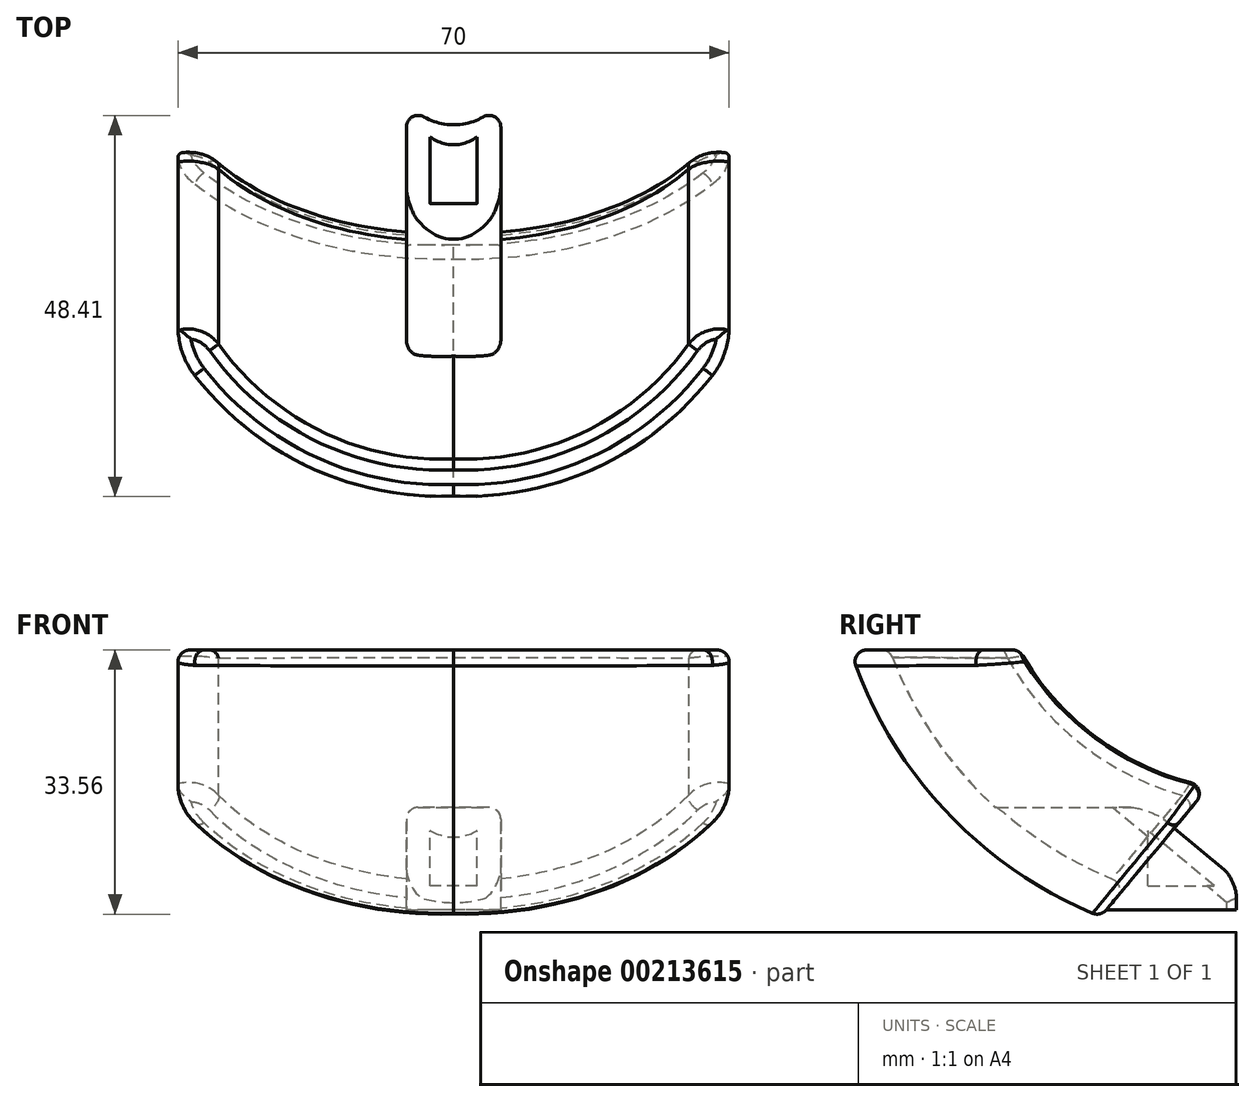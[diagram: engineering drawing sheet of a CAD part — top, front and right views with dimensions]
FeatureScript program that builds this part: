
annotation { "Feature Type Name" : "Feature", "Feature Type Description" : "" }
export const myFeature = defineFeature(function(context is Context, id is Id, definition is map)
    precondition{}
    {
        {
            var Q0;
            Q0=qCreatedBy(makeId("Right.planeOp"),FACE);
            var sketch = newSketch(context, id + "F0", { "sketchPlane" : qUnion([Q0])});
            skLineSegment(sketch, "E0.bottom", {"start": v(0, 0) * mm, "end": v(30, 0) * mm, "construction": true});
            skLineSegment(sketch, "E0.left", {"start": v(0, 0) * mm, "end": v(0, 30) * mm, "construction": true});
            skArc(sketch, "E1", {"start": v(0, 30) * mm, "mid": v(11.66, 11.66) * mm, "end": v(30, 0) * mm});
            skPoint(sketch, "E2", {"position": v(13.08, 10.3) * mm});
            skPoint(sketch, "E3", {"position": v(-15, 30) * mm});
            skPoint(sketch, "E4", {"position": v(3.08, 10.3) * mm});
            skPoint(sketch, "E5", {"position": v(30, 0) * mm});
            skPoint(sketch, "E6", {"position": v(25, 0) * mm});
            skFitSpline(sketch, "E7", {"points": [v(-15, 30) * mm, v(25, 0) * mm, v(100.66, 9.32) * mm], "startDerivative": vector(35.39, -77.1) * mm, "endDerivative": vector(150.07, 40.05) * mm});
            skSolve(sketch);
        }
        {
            var Q0;
            Q0=sQuery(id+"F0.wireOp",VERTEX,"E1.start");
            var Q1;
            Q1=qCreatedBy(makeId("Top.planeOp"),FACE);
            cPlane(context, id + "F1", {"entities" : qUnion([Q0, Q1]), "cplaneType" : CPlaneType.PLANE_POINT, "offset" : 25 * mm, "width" : 150 * mm, "height" : 150 * mm});
        }
        {
            var Q0;
            Q0=qCreatedBy(id+"F1.planeOp",FACE);
            var sketch = newSketch(context, id + "F2", { "sketchPlane" : qUnion([Q0])});
            skArc(sketch, "E8", {"start": v(-35, 24.67) * mm, "mid": v(-21.71, 6.36) * mm, "end": v(0, 0) * mm});
            skArc(sketch, "E9", {"start": v(0, 0) * mm, "mid": v(21.71, 6.36) * mm, "end": v(35, 24.67) * mm});
            skLineSegment(sketch, "E10", {"start": v(-35, 24.67) * mm, "end": v(-35, 16.25) * mm});
            skArc(sketch, "E11.0", {"start": v(0, -5) * mm, "mid": v(18.2, -1.4) * mm, "end": v(32.82, 10.02) * mm});
            skArc(sketch, "E11.1", {"start": v(-32.82, 10.02) * mm, "mid": v(-18.2, -1.4) * mm, "end": v(0, -5) * mm});
            skLineSegment(sketch, "E12", {"start": v(35, 24.67) * mm, "end": v(35, 16.25) * mm});
            skEllipticalArc(sketch, "E13", {});
            skPoint(sketch, "E14.visualSharp", {"position": v(-35, 13.03) * mm});
            skArc(sketch, "E14.filletArc", {"start": v(-35, 16.25) * mm, "mid": v(-34.44, 12.95) * mm, "end": v(-32.82, 10.02) * mm});
            skPoint(sketch, "E15.visualSharp", {"position": v(35, 13.03) * mm});
            skArc(sketch, "E15.filletArc", {"start": v(32.82, 10.02) * mm, "mid": v(34.44, 12.95) * mm, "end": v(35, 16.25) * mm});
            skEllipticalArc(sketch, "E16.trimOffspring", {});
            skPoint(sketch, "E17.orphan", {"position": v(0, -15) * mm});
            const initialGuessF2  = {"E13": [0, -0.005004295268239853, 0, -1, 0.01, 0.00424685629998106, 4.184836836168355, 4.7062911756630585], "E16.trimOffspring": [0, -0.005004295268239853, 0, -1, 0.01, 0.00424685629998106, 1.576894131516556, 2.098348471011326]};
            skSetInitialGuess(sketch, initialGuessF2);
            skSolve(sketch);
        }
        {
            var Q0;
            Q0=sQuery(id+"F0.wireOp",VERTEX,"E2");
            var Q1;
            Q1=qCreatedBy(makeId("Top.planeOp"),FACE);
            cPlane(context, id + "F3", {"entities" : qUnion([Q0, Q1]), "cplaneType" : CPlaneType.PLANE_POINT, "offset" : 25 * mm, "width" : 150 * mm, "height" : 150 * mm});
        }
        {
            var Q0;
            {var subQ5=sQuery(id+"F2.wireOp",EDGE,"E10");Q0=makeQuery(id+"F2.imprint","IMPRINT",FACE,{"disambiguationData":[TD([[makeQuery(id+"F2.imprint","IMPRINT",EDGE,{"derivedFrom":subQ5}),1.0]])]});}
            var Q1;
            {var subQ6=sQuery(id+"F2.wireOp",EDGE,"E9");var subQ7=sQuery(id+"F2.wireOp",EDGE,"E8");var subQ8=makeQuery(id+"F2.imprint","INTERSECT",VERTEX,{"derivedFrom":[subQ7,subQ6]});Q1=makeQuery(id+"F2.imprint","IMPRINT",FACE,{"disambiguationData":[TD([[makeQuery(id+"F2.imprint","IMPRINT",EDGE,{"disambiguationData":[TD([[subQ8,1.0]])],"derivedFrom":subQ7}),-1.0]])]});}
            var Q2;
            {var subQ5=sQuery(id+"F2.wireOp",EDGE,"E12");Q2=makeQuery(id+"F2.imprint","IMPRINT",FACE,{"disambiguationData":[TD([[makeQuery(id+"F2.imprint","IMPRINT",EDGE,{"derivedFrom":subQ5}),-1.0]])]});}
            var Q3;
            {var subQ0=sQuery(id+"F2.wireOp",EDGE,"lZaFmeEu-P24d-Nwwk-X734-4g5lw6kWDEKw");Q3=makeQuery(id+"F2.imprint","IMPRINT",FACE,{"disambiguationData":[TD([[makeQuery(id+"F2.imprint","IMPRINT",EDGE,{"derivedFrom":subQ0}),1.0]])]});}
            var Q4;
            {var subQ0=sQuery(id+"F2.wireOp",EDGE,"lZaFmeEu-P24d-Nwwk-X734-4g5lw6kWDEKw");Q4=makeQuery(id+"F2.imprint","IMPRINT",FACE,{"disambiguationData":[TD([[makeQuery(id+"F2.imprint","IMPRINT",EDGE,{"derivedFrom":subQ0}),-1.0]])]});}
            var Q5;
            Q5=sQuery(id+"F0.wireOp",EDGE,"E1");
            sweep(context, id + "F4", {"profiles" : qUnion([Q0, Q1, Q2, Q3, Q4]), "path" : qUnion([Q5])});
        }
        {
            var Q0;
            Q0=qCreatedBy(makeId("Front.planeOp"),FACE);
            var Q1;
            Q1=makeQuery(id+"F4.opSweep","CAP_VERTEX",VERTEX,{"disambiguationData":[OSD([sQuery(id+"F0.wireOp",EDGE,"E1"),sQuery(id+"F2.wireOp",EDGE,"E9"),sQuery(id+"F2.wireOp",EDGE,"E12")])],"isStart":false});
            cPlane(context, id + "F5", {"entities" : qUnion([Q0, Q1]), "cplaneType" : CPlaneType.PLANE_POINT, "offset" : 25 * mm, "width" : 150 * mm, "height" : 150 * mm});
        }
        {
            var Q0;
            Q0=qCreatedBy(id+"F5.planeOp",FACE);
            var sketch = newSketch(context, id + "F6", { "sketchPlane" : qUnion([Q0])});
            skLineSegment(sketch, "E18.bottom", {"start": v(3, 0) * mm, "end": v(-3, 0) * mm});
            skLineSegment(sketch, "E18.top", {"start": v(3, 7) * mm, "end": v(-3, 7) * mm});
            skLineSegment(sketch, "E18.left", {"start": v(3, 0) * mm, "end": v(3, 7) * mm});
            skLineSegment(sketch, "E18.right", {"start": v(-3, 0) * mm, "end": v(-3, 7) * mm});
            skPoint(sketch, "E18.middle", {"position": v(0, 3.5) * mm});
            skLineSegment(sketch, "E19.0", {"start": v(6, 10) * mm, "end": v(-6, 10) * mm});
            skLineSegment(sketch, "E19.1", {"start": v(6, -3) * mm, "end": v(6, 10) * mm});
            skLineSegment(sketch, "E19.2", {"start": v(6, -3) * mm, "end": v(-6, -3) * mm});
            skLineSegment(sketch, "E19.3", {"start": v(-6, -3) * mm, "end": v(-6, 10) * mm});
            skSolve(sketch);
        }
        {
            var Q0;
            Q0=makeQuery(id+"F6.imprint","IMPRINT",FACE,{"disambiguationData":[TD([[makeQuery(id+"F6.imprint","IMPRINT",EDGE,{"derivedFrom":sQuery(id+"F6.wireOp",EDGE,"E18.bottom")}),1.0]])]});
            var Q1;
            Q1=makeQuery(id+"F6.imprint","IMPRINT",FACE,{"disambiguationData":[TD([[makeQuery(id+"F6.imprint","IMPRINT",EDGE,{"derivedFrom":sQuery(id+"F6.wireOp",EDGE,"E18.bottom")}),-1.0]])]});
            extrude(context, id + "F7", {"entities" : qUnion([Q0, Q1]), "operationType" : NewBodyOperationType.ADD, "endBound" : BoundingType.UP_TO_NEXT, "depth" : 25 * mm});
        }
        {
            var Q0;
            Q0=makeQuery(id+"F6.imprint","IMPRINT",FACE,{"disambiguationData":[TD([[makeQuery(id+"F6.imprint","IMPRINT",EDGE,{"derivedFrom":sQuery(id+"F6.wireOp",EDGE,"E18.bottom")}),-1.0]])]});
            extrude(context, id + "F8", {"entities" : qUnion([Q0]), "operationType" : NewBodyOperationType.REMOVE, "depth" : 13 * mm});
        }
        {
            var Q0;
            Q0=makeQuery(id+"F7.opExtrude","SWEPT_FACE",FACE,{"disambiguationData":[OSD([sQuery(id+"F6.wireOp",EDGE,"E19.0")])]});
            var sketch = newSketch(context, id + "F9", { "sketchPlane" : qUnion([Q0])});
            skArc(sketch, "E20", {"start": v(-6, 45.79) * mm, "mid": v(0, 42.79) * mm, "end": v(6, 45.79) * mm});
            skLineSegment(sketch, "E21", {"start": v(-6, 45.79) * mm, "end": v(6, 45.79) * mm});
            skSolve(sketch);
        }
        {
            var Q0;
            Q0=qSketchRegion(id+"F9",true);
            extrude(context, id + "F10", {"entities" : qUnion([Q0]), "operationType" : NewBodyOperationType.REMOVE, "endBound" : BoundingType.THROUGH_ALL, "oppositeDirection" : true, "depth" : 25 * mm});
        }
        {
            var Q0;
            Q0=makeQuery(id+"F4.opSweep","SWEPT_EDGE",EDGE,{"disambiguationData":[OSD([sQuery(id+"F0.wireOp",EDGE,"E1"),sQuery(id+"F2.wireOp",EDGE,"E8"),sQuery(id+"F2.wireOp",EDGE,"E10")])]});
            var Q1;
            Q1=makeQuery(id+"F4.opSweep","SWEPT_EDGE",EDGE,{"disambiguationData":[OSD([sQuery(id+"F0.wireOp",EDGE,"E1"),sQuery(id+"F2.wireOp",EDGE,"E9"),sQuery(id+"F2.wireOp",EDGE,"E12")])]});
            fillet(context, id + "F11", {"entities" : qUnion([Q0, Q1]), "radius" : 5 * mm, "tangentPropagation" : true, "allowEdgeOverflow" : false});
        }
        {
            var Q0;
            Q0=makeQuery(id+"F4.opSweep","CAP_EDGE",EDGE,{"disambiguationData":[OSD([sQuery(id+"F0.wireOp",VERTEX,"E1.start"),sQuery(id+"F2.wireOp",EDGE,"E11.0")])],"isStart":true});
            var Q1;
            Q1=makeQuery(id+"F4.opSweep","CAP_EDGE",EDGE,{"disambiguationData":[OSD([sQuery(id+"F0.wireOp",VERTEX,"E1.start"),sQuery(id+"F2.wireOp",EDGE,"E11.1")])],"isStart":true});
            var Q2;
            Q2=makeQuery(id+"F4.opSweep","CAP_EDGE",EDGE,{"disambiguationData":[OSD([sQuery(id+"F0.wireOp",VERTEX,"E1.end"),sQuery(id+"F2.wireOp",EDGE,"E11.0")])],"isStart":false});
            var Q3;
            Q3=makeQuery(id+"F4.opSweep","CAP_EDGE",EDGE,{"disambiguationData":[OSD([sQuery(id+"F0.wireOp",VERTEX,"E1.end"),sQuery(id+"F2.wireOp",EDGE,"E11.1")])],"isStart":false});
            var Q4;
            Q4=makeQuery(id+"F4.opSweep","CAP_EDGE",EDGE,{"disambiguationData":[OSD([sQuery(id+"F0.wireOp",VERTEX,"E1.end"),sQuery(id+"F2.wireOp",EDGE,"E9")])],"isStart":false});
            var Q5;
            Q5=makeQuery(id+"F4.opSweep","CAP_EDGE",EDGE,{"disambiguationData":[OSD([sQuery(id+"F0.wireOp",VERTEX,"E1.end"),sQuery(id+"F2.wireOp",EDGE,"E8")])],"isStart":false});
            var Q6;
            Q6=makeQuery(id+"F4.opSweep","CAP_EDGE",EDGE,{"disambiguationData":[OSD([sQuery(id+"F0.wireOp",VERTEX,"E1.start"),sQuery(id+"F2.wireOp",EDGE,"E8")])],"isStart":true});
            var Q7;
            {var subQ0=sQuery(id+"F2.wireOp",EDGE,"E12");var subQ1=sQuery(id+"F2.wireOp",EDGE,"E9");Q7=makeQuery(id+"F11.opFillet","BLEND_EDGE",EDGE,{"blendedFrom":[makeQuery(id+"F4.opSweep","SWEPT_EDGE",EDGE,{"disambiguationData":[OSD([sQuery(id+"F0.wireOp",EDGE,"E1"),subQ1,subQ0])]}),makeQuery(id+"F4.opSweep","CAP_FACE",FACE,{"disambiguationData":[OSD([sQuery(id+"F0.wireOp",VERTEX,"E1.start"),sQuery(id+"F2.wireOp",EDGE,"E8"),subQ1,sQuery(id+"F2.wireOp",EDGE,"E10"),sQuery(id+"F2.wireOp",EDGE,"E11.0"),sQuery(id+"F2.wireOp",EDGE,"E11.1"),subQ0,sQuery(id+"F2.wireOp",EDGE,"E14.filletArc"),sQuery(id+"F2.wireOp",EDGE,"E15.filletArc")])],"isStart":true})],"blendedInto":[makeQuery(id+"F4.opSweep","CAP_FACE",FACE,{"disambiguationData":[OSD([sQuery(id+"F0.wireOp",VERTEX,"E1.start"),sQuery(id+"F2.wireOp",EDGE,"E8"),subQ1,sQuery(id+"F2.wireOp",EDGE,"E10"),sQuery(id+"F2.wireOp",EDGE,"E11.0"),sQuery(id+"F2.wireOp",EDGE,"E11.1"),subQ0,sQuery(id+"F2.wireOp",EDGE,"E14.filletArc"),sQuery(id+"F2.wireOp",EDGE,"E15.filletArc")])],"isStart":true})]});}
            var Q8;
            Q8=makeQuery(id+"F7.opExtrude","SWEPT_EDGE",EDGE,{"disambiguationData":[OSD([sQuery(id+"F6.wireOp",EDGE,"E19.0"),sQuery(id+"F6.wireOp",EDGE,"E19.1")])]});
            var Q9;
            Q9=makeQuery(id+"F7.opExtrude","SWEPT_EDGE",EDGE,{"disambiguationData":[OSD([sQuery(id+"F6.wireOp",EDGE,"E19.0"),sQuery(id+"F6.wireOp",EDGE,"E19.3")])]});
            var Q10;
            {var subQ0=sQuery(id+"F6.wireOp",EDGE,"E19.1");Q10=makeQuery(id+"F10.boolean.opBoolean","MERGE",EDGE,{"derivedFrom":[makeQuery(id+"F7.opExtrude","CAP_EDGE",EDGE,{"disambiguationData":[OSD([subQ0])],"isStart":true}),makeQuery(id+"F10.opExtrude","SWEPT_EDGE",EDGE,{"disambiguationData":[OSD([sQuery(id+"F6.wireOp",EDGE,"E19.0"),subQ0,sQuery(id+"F9.wireOp",EDGE,"E20"),sQuery(id+"F9.wireOp",EDGE,"E21")])]})]});}
            var Q11;
            {var subQ0=sQuery(id+"F6.wireOp",EDGE,"E19.3");Q11=makeQuery(id+"F10.boolean.opBoolean","MERGE",EDGE,{"derivedFrom":[makeQuery(id+"F7.opExtrude","CAP_EDGE",EDGE,{"disambiguationData":[OSD([subQ0])],"isStart":true}),makeQuery(id+"F10.opExtrude","SWEPT_EDGE",EDGE,{"disambiguationData":[OSD([sQuery(id+"F6.wireOp",EDGE,"E19.0"),subQ0,sQuery(id+"F9.wireOp",EDGE,"E20"),sQuery(id+"F9.wireOp",EDGE,"E21")])]})]});}
            fillet(context, id + "F12", {"entities" : qUnion([Q0, Q1, Q2, Q3, Q4, Q5, Q6, Q7, Q8, Q9, Q10, Q11]), "radius" : 1.5 * mm, "tangentPropagation" : true, "allowEdgeOverflow" : false});
        }
        {
            var Q0;
            Q0=makeQuery(id+"F12.opFillet","SPLIT",FACE,{"disambiguationData":[OD(1.0)],"derivedFrom":makeQuery(id+"F4.opSweep","CAP_FACE",FACE,{"disambiguationData":[OSD([sQuery(id+"F0.wireOp",VERTEX,"E1.end"),sQuery(id+"F2.wireOp",EDGE,"E8"),sQuery(id+"F2.wireOp",EDGE,"E9"),sQuery(id+"F2.wireOp",EDGE,"E10"),sQuery(id+"F2.wireOp",EDGE,"E11.0"),sQuery(id+"F2.wireOp",EDGE,"E11.1"),sQuery(id+"F2.wireOp",EDGE,"E12"),sQuery(id+"F2.wireOp",EDGE,"E14.filletArc"),sQuery(id+"F2.wireOp",EDGE,"E15.filletArc")])],"isStart":false})});
            cPlane(context, id + "F13", {"entities" : qUnion([Q0]), "cplaneType" : CPlaneType.OFFSET, "offset" : 25 * mm, "oppositeDirection" : true, "width" : 150 * mm, "height" : 150 * mm});
        }
        {
            var Q0;
            Q0=qCreatedBy(id+"F13.planeOp",FACE);
            var sketch = newSketch(context, id + "F14", { "sketchPlane" : qUnion([Q0])});
            skLineSegment(sketch, "E22", {"start": v(0, 35.07) * mm, "end": v(0, 25.77) * mm, "construction": true});
            skLineSegment(sketch, "E23", {"start": v(6, 25.77) * mm, "end": v(6, 38.07) * mm});
            skLineSegment(sketch, "E24.MirrorCS", {"start": v(-6, 25.77) * mm, "end": v(-6, 38.07) * mm});
            skPoint(sketch, "E25", {"position": v(6, 28.77) * mm});
            skPoint(sketch, "E26.MirrorP", {"position": v(-6, 28.77) * mm});
            skArc(sketch, "E27", {"start": v(-6, 28.77) * mm, "mid": v(0, 25.77) * mm, "end": v(6, 28.77) * mm});
            skLineSegment(sketch, "E28", {"start": v(6, 38.07) * mm, "end": v(-6, 38.07) * mm});
            skSolve(sketch);
        }
        {
            var Q0;
            Q0 = qSketchRegion(id + "F14", true);
            extrude(context, id + "F15", {"entities" : qUnion([Q0]), "operationType" : NewBodyOperationType.REMOVE, "endBound" : BoundingType.THROUGH_ALL, "depth" : 25 * mm});
        }
    });
